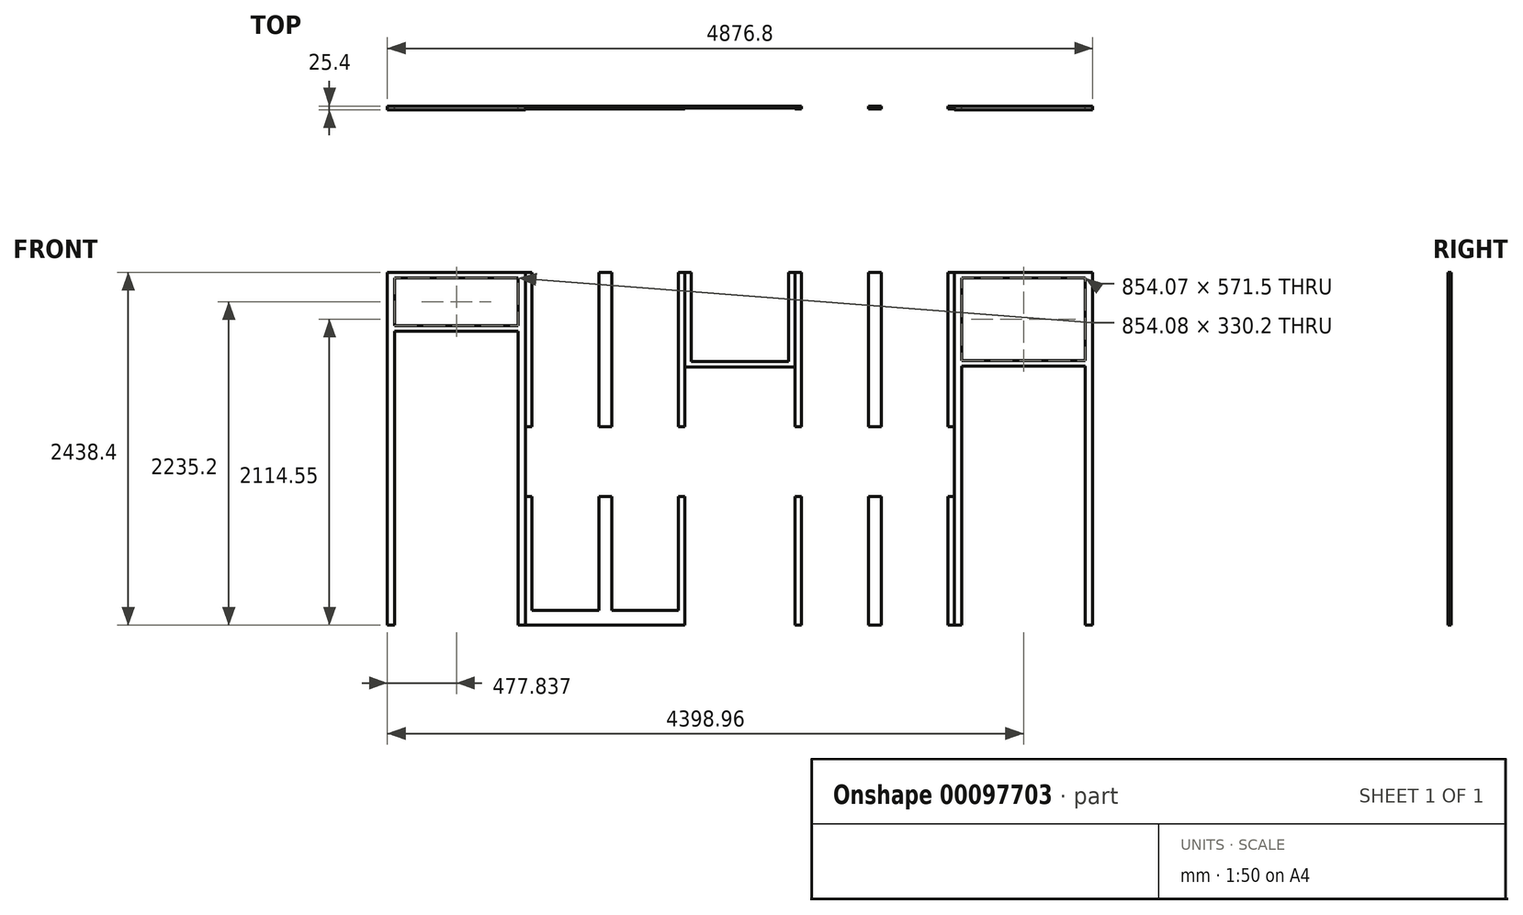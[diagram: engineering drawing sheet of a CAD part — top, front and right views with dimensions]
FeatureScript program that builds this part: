
annotation { "Feature Type Name" : "Feature", "Feature Type Description" : "" }
export const myFeature = defineFeature(function(context is Context, id is Id, definition is map)
    precondition{}
    {
        {
            var Q0;
            Q0=qCreatedBy(makeId("Front.planeOp"),FACE);
            var sketch = newSketch(context, id + "F0", { "sketchPlane" : qUnion([Q0])});
            skLineSegment(sketch, "E0.bottom", {"start": v(0, 0) * mm, "end": v(4876.8, 0) * mm});
            skLineSegment(sketch, "E0.top", {"start": v(0, 2438.4) * mm, "end": v(4876.8, 2438.4) * mm});
            skLineSegment(sketch, "E0.left", {"start": v(0, 0) * mm, "end": v(0, 2438.4) * mm});
            skLineSegment(sketch, "E0.right", {"start": v(4876.8, 0) * mm, "end": v(4876.8, 2438.4) * mm});
            skLineSegment(sketch, "E1", {"start": v(3971.92, 2438.4) * mm, "end": v(3971.92, 0) * mm});
            skLineSegment(sketch, "E2.0", {"start": v(3921.12, 2438.4) * mm, "end": v(3921.12, 0) * mm});
            skLineSegment(sketch, "E3.0", {"start": v(4826, 0) * mm, "end": v(4826, 2438.4) * mm});
            skLineSegment(sketch, "E4", {"start": v(3971.92, 1790.7) * mm, "end": v(4826, 1790.7) * mm});
            skLineSegment(sketch, "E5.0", {"start": v(3971.92, 1828.8) * mm, "end": v(4826, 1828.8) * mm});
            skLineSegment(sketch, "E6", {"start": v(3971.93, 2400.3) * mm, "end": v(4826, 2400.3) * mm});
            skLineSegment(sketch, "E7", {"start": v(3876.67, 0) * mm, "end": v(3876.67, 889) * mm});
            skLineSegment(sketch, "E8", {"start": v(3876.67, 889) * mm, "end": v(3921.13, 889) * mm});
            skLineSegment(sketch, "E9", {"start": v(2438.4, 0) * mm, "end": v(2438.4, 2578.54) * mm, "construction": true});
            skLineSegment(sketch, "E10", {"start": v(2057.4, 0) * mm, "end": v(2057.4, 914.4) * mm});
            skLineSegment(sketch, "E11", {"start": v(2057.4, 914.4) * mm, "end": v(2819.4, 914.4) * mm});
            skLineSegment(sketch, "E12", {"start": v(2819.4, 914.4) * mm, "end": v(2819.4, 0) * mm});
            skLineSegment(sketch, "E13", {"start": v(2819.4, 889) * mm, "end": v(2863.85, 889) * mm});
            skLineSegment(sketch, "E14", {"start": v(2863.85, 889) * mm, "end": v(2863.85, 0) * mm});
            skLineSegment(sketch, "E15", {"start": v(3414.71, 0) * mm, "end": v(3414.71, 889) * mm});
            skLineSegment(sketch, "E16", {"start": v(3325.81, 889) * mm, "end": v(3414.71, 889) * mm});
            skLineSegment(sketch, "E17", {"start": v(3325.81, 889) * mm, "end": v(3325.81, 0) * mm});
            skLineSegment(sketch, "E18", {"start": v(50.8, 0) * mm, "end": v(50.8, 2438.4) * mm});
            skLineSegment(sketch, "E19", {"start": v(50.8, 2032) * mm, "end": v(904.87, 2032) * mm});
            skLineSegment(sketch, "E20", {"start": v(904.87, 2438.4) * mm, "end": v(904.87, 0) * mm});
            skLineSegment(sketch, "E21.0", {"start": v(50.8, 2070.1) * mm, "end": v(904.87, 2070.1) * mm});
            skLineSegment(sketch, "E22.0", {"start": v(955.67, 2438.4) * mm, "end": v(955.67, 0) * mm});
            skLineSegment(sketch, "E23", {"start": v(1000.12, 101.6) * mm, "end": v(1000.12, 889) * mm});
            skLineSegment(sketch, "E24", {"start": v(1000.12, 889) * mm, "end": v(955.68, 889) * mm});
            skLineSegment(sketch, "E25", {"start": v(2012.95, 0) * mm, "end": v(2012.95, 889) * mm});
            skLineSegment(sketch, "E26", {"start": v(2012.95, 889) * mm, "end": v(2057.4, 889) * mm});
            skLineSegment(sketch, "E27", {"start": v(1550.99, 101.6) * mm, "end": v(1550.99, 889) * mm});
            skLineSegment(sketch, "E28", {"start": v(1462.09, 889) * mm, "end": v(1550.99, 889) * mm});
            skLineSegment(sketch, "E29", {"start": v(1462.09, 889) * mm, "end": v(1462.09, 101.6) * mm});
            skLineSegment(sketch, "E30", {"start": v(1000.12, 889) * mm, "end": v(1550.99, 889) * mm, "construction": true});
            skLineSegment(sketch, "E31", {"start": v(1462.09, 889) * mm, "end": v(2012.95, 889) * mm, "construction": true});
            skLineSegment(sketch, "E32", {"start": v(2863.85, 889) * mm, "end": v(3325.81, 889) * mm, "construction": true});
            skLineSegment(sketch, "E33", {"start": v(3414.71, 889) * mm, "end": v(3876.67, 889) * mm, "construction": true});
            skLineSegment(sketch, "E34", {"start": v(1000.12, 101.6) * mm, "end": v(2012.95, 101.6) * mm});
            skLineSegment(sketch, "E35", {"start": v(50.8, 2400.3) * mm, "end": v(904.87, 2400.3) * mm});
            skPoint(sketch, "E36.orphan", {"position": v(1462.09, 0) * mm});
            skLineSegment(sketch, "E37", {"start": v(1000.12, 2438.4) * mm, "end": v(1000.12, 1371.6) * mm});
            skLineSegment(sketch, "E38", {"start": v(1000.12, 1371.6) * mm, "end": v(955.67, 1371.6) * mm});
            skLineSegment(sketch, "E39", {"start": v(1462.09, 1371.6) * mm, "end": v(1462.09, 2438.4) * mm});
            skLineSegment(sketch, "E40", {"start": v(1462.09, 1371.6) * mm, "end": v(1550.99, 1371.6) * mm});
            skLineSegment(sketch, "E41", {"start": v(1550.99, 1371.6) * mm, "end": v(1550.99, 2438.4) * mm});
            skLineSegment(sketch, "E42", {"start": v(2012.95, 1371.6) * mm, "end": v(2012.95, 2438.4) * mm});
            skLineSegment(sketch, "E43", {"start": v(2012.95, 1371.6) * mm, "end": v(2057.4, 1371.6) * mm});
            skLineSegment(sketch, "E44", {"start": v(2057.4, 1371.6) * mm, "end": v(2057.4, 2438.4) * mm});
            skLineSegment(sketch, "E45", {"start": v(2057.4, 1784.35) * mm, "end": v(2819.4, 1784.35) * mm});
            skLineSegment(sketch, "E46.0", {"start": v(2057.4, 1822.45) * mm, "end": v(2819.4, 1822.45) * mm});
            skLineSegment(sketch, "E47", {"start": v(2819.4, 1371.6) * mm, "end": v(2819.4, 2438.4) * mm});
            skLineSegment(sketch, "E48", {"start": v(2819.4, 1371.6) * mm, "end": v(2863.85, 1371.6) * mm});
            skLineSegment(sketch, "E49", {"start": v(2863.85, 1371.6) * mm, "end": v(2863.85, 2438.4) * mm});
            skLineSegment(sketch, "E50", {"start": v(2774.95, 1822.45) * mm, "end": v(2774.95, 2438.4) * mm});
            skLineSegment(sketch, "E51", {"start": v(2101.85, 1822.45) * mm, "end": v(2101.85, 2438.4) * mm});
            skLineSegment(sketch, "E52", {"start": v(3325.81, 1371.6) * mm, "end": v(3325.81, 2438.4) * mm});
            skLineSegment(sketch, "E53", {"start": v(3325.81, 1371.6) * mm, "end": v(3414.71, 1371.6) * mm});
            skLineSegment(sketch, "E54", {"start": v(3414.71, 1371.6) * mm, "end": v(3414.71, 2438.4) * mm});
            skLineSegment(sketch, "E55", {"start": v(3876.67, 1371.6) * mm, "end": v(3876.67, 2438.4) * mm});
            skLineSegment(sketch, "E56", {"start": v(3876.67, 1371.6) * mm, "end": v(3921.12, 1371.6) * mm});
            skSolve(sketch);
        }
        {
            var Q0;
            {var subQ4=sQuery(id+"F0.wireOp",EDGE,"E0.left");Q0=makeQuery(id+"F0.imprint","IMPRINT",FACE,{"disambiguationData":[TD([[makeQuery(id+"F0.imprint","IMPRINT",EDGE,{"derivedFrom":subQ4}),-1.0]])]});}
            var Q1;
            {var subQ0=sQuery(id+"F0.wireOp",EDGE,"E19");Q1=makeQuery(id+"F0.imprint","IMPRINT",FACE,{"disambiguationData":[TD([[makeQuery(id+"F0.imprint","IMPRINT",EDGE,{"derivedFrom":subQ0}),1.0]])]});}
            var Q2;
            {var subQ5=sQuery(id+"F0.wireOp",EDGE,"E35");Q2=makeQuery(id+"F0.imprint","IMPRINT",FACE,{"disambiguationData":[TD([[makeQuery(id+"F0.imprint","IMPRINT",EDGE,{"derivedFrom":subQ5}),1.0]])]});}
            var Q3;
            {var subQ0=sQuery(id+"F0.wireOp",EDGE,"E20");var subQ8=sQuery(id+"F0.wireOp",EDGE,"E0.bottom");var subQ11=makeQuery(id+"F0.imprint","INTERSECT",VERTEX,{"derivedFrom":[subQ8,subQ0]});Q3=makeQuery(id+"F0.imprint","IMPRINT",FACE,{"disambiguationData":[TD([[makeQuery(id+"F0.imprint","IMPRINT",EDGE,{"disambiguationData":[TD([[subQ11,-1.0]])],"derivedFrom":subQ8}),1.0]])]});}
            var Q4;
            {var subQ0=sQuery(id+"F0.wireOp",EDGE,"E1");var subQ7=sQuery(id+"F0.wireOp",EDGE,"E0.bottom");var subQ10=makeQuery(id+"F0.imprint","INTERSECT",VERTEX,{"derivedFrom":[subQ7,subQ0]});Q4=makeQuery(id+"F0.imprint","IMPRINT",FACE,{"disambiguationData":[TD([[makeQuery(id+"F0.imprint","IMPRINT",EDGE,{"disambiguationData":[TD([[subQ10,1.0]])],"derivedFrom":subQ7}),1.0]])]});}
            var Q5;
            {var subQ0=sQuery(id+"F0.wireOp",EDGE,"E4");Q5=makeQuery(id+"F0.imprint","IMPRINT",FACE,{"disambiguationData":[TD([[makeQuery(id+"F0.imprint","IMPRINT",EDGE,{"derivedFrom":subQ0}),1.0]])]});}
            var Q6;
            {var subQ5=sQuery(id+"F0.wireOp",EDGE,"E6");Q6=makeQuery(id+"F0.imprint","IMPRINT",FACE,{"disambiguationData":[TD([[makeQuery(id+"F0.imprint","IMPRINT",EDGE,{"derivedFrom":subQ5}),1.0]])]});}
            var Q7;
            {var subQ0=sQuery(id+"F0.wireOp",EDGE,"E0.right");Q7=makeQuery(id+"F0.imprint","IMPRINT",FACE,{"disambiguationData":[TD([[makeQuery(id+"F0.imprint","IMPRINT",EDGE,{"derivedFrom":subQ0}),1.0]])]});}
            extrude(context, id + "F1", {"entities" : qUnion([Q0, Q1, Q2, Q3, Q4, Q5, Q6, Q7]), "depth" : 25.4 * mm});
        }
        {
            var Q0;
            {var subQ3=sQuery(id+"F0.wireOp",EDGE,"E37");Q0=makeQuery(id+"F0.imprint","IMPRINT",FACE,{"disambiguationData":[TD([[makeQuery(id+"F0.imprint","IMPRINT",EDGE,{"derivedFrom":subQ3}),-1.0]])]});}
            var Q1;
            {var subQ0=sQuery(id+"F0.wireOp",EDGE,"E39");Q1=makeQuery(id+"F0.imprint","IMPRINT",FACE,{"disambiguationData":[TD([[makeQuery(id+"F0.imprint","IMPRINT",EDGE,{"derivedFrom":subQ0}),-1.0]])]});}
            var Q2;
            {var subQ3=sQuery(id+"F0.wireOp",EDGE,"E42");Q2=makeQuery(id+"F0.imprint","IMPRINT",FACE,{"disambiguationData":[TD([[makeQuery(id+"F0.imprint","IMPRINT",EDGE,{"derivedFrom":subQ3}),-1.0]])]});}
            var Q3;
            {var subQ6=sQuery(id+"F0.wireOp",EDGE,"E48");Q3=makeQuery(id+"F0.imprint","IMPRINT",FACE,{"disambiguationData":[TD([[makeQuery(id+"F0.imprint","IMPRINT",EDGE,{"derivedFrom":subQ6}),1.0]])]});}
            var Q4;
            {var subQ0=sQuery(id+"F0.wireOp",EDGE,"E52");Q4=makeQuery(id+"F0.imprint","IMPRINT",FACE,{"disambiguationData":[TD([[makeQuery(id+"F0.imprint","IMPRINT",EDGE,{"derivedFrom":subQ0}),-1.0]])]});}
            var Q5;
            {var subQ3=sQuery(id+"F0.wireOp",EDGE,"E55");Q5=makeQuery(id+"F0.imprint","IMPRINT",FACE,{"disambiguationData":[TD([[makeQuery(id+"F0.imprint","IMPRINT",EDGE,{"derivedFrom":subQ3}),-1.0]])]});}
            var Q6;
            {var subQ1=sQuery(id+"F0.wireOp",EDGE,"E23");Q6=makeQuery(id+"F0.imprint","IMPRINT",FACE,{"disambiguationData":[TD([[makeQuery(id+"F0.imprint","IMPRINT",EDGE,{"derivedFrom":subQ1}),1.0]])]});}
            var Q7;
            {var subQ0=sQuery(id+"F0.wireOp",EDGE,"E27");Q7=makeQuery(id+"F0.imprint","IMPRINT",FACE,{"disambiguationData":[TD([[makeQuery(id+"F0.imprint","IMPRINT",EDGE,{"derivedFrom":subQ0}),1.0]])]});}
            var Q8;
            {var subQ0=sQuery(id+"F0.wireOp",EDGE,"E26");Q8=makeQuery(id+"F0.imprint","IMPRINT",FACE,{"disambiguationData":[TD([[makeQuery(id+"F0.imprint","IMPRINT",EDGE,{"derivedFrom":subQ0}),-1.0]])]});}
            var Q9;
            {var subQ4=sQuery(id+"F0.wireOp",EDGE,"E13");Q9=makeQuery(id+"F0.imprint","IMPRINT",FACE,{"disambiguationData":[TD([[makeQuery(id+"F0.imprint","IMPRINT",EDGE,{"derivedFrom":subQ4}),-1.0]])]});}
            var Q10;
            {var subQ0=sQuery(id+"F0.wireOp",EDGE,"E15");Q10=makeQuery(id+"F0.imprint","IMPRINT",FACE,{"disambiguationData":[TD([[makeQuery(id+"F0.imprint","IMPRINT",EDGE,{"derivedFrom":subQ0}),1.0]])]});}
            var Q11;
            {var subQ3=sQuery(id+"F0.wireOp",EDGE,"E7");Q11=makeQuery(id+"F0.imprint","IMPRINT",FACE,{"disambiguationData":[TD([[makeQuery(id+"F0.imprint","IMPRINT",EDGE,{"derivedFrom":subQ3}),-1.0]])]});}
            extrude(context, id + "F2", {"entities" : qUnion([Q0, Q1, Q2, Q3, Q4, Q5, Q6, Q7, Q8, Q9, Q10, Q11]), "depth" : 19.05 * mm});
        }
        {
            var Q0;
            {var subQ3=sQuery(id+"F0.wireOp",EDGE,"E51");Q0=makeQuery(id+"F0.imprint","IMPRINT",FACE,{"disambiguationData":[TD([[makeQuery(id+"F0.imprint","IMPRINT",EDGE,{"derivedFrom":subQ3}),1.0]])]});}
            var Q1;
            {var subQ5=sQuery(id+"F0.wireOp",EDGE,"E45");Q1=makeQuery(id+"F0.imprint","IMPRINT",FACE,{"disambiguationData":[TD([[makeQuery(id+"F0.imprint","IMPRINT",EDGE,{"derivedFrom":subQ5}),1.0]])]});}
            var Q2;
            {var subQ3=sQuery(id+"F0.wireOp",EDGE,"E50");Q2=makeQuery(id+"F0.imprint","IMPRINT",FACE,{"disambiguationData":[TD([[makeQuery(id+"F0.imprint","IMPRINT",EDGE,{"derivedFrom":subQ3}),-1.0]])]});}
            extrude(context, id + "F3", {"entities" : qUnion([Q0, Q1, Q2]), "depth" : 12.7 * mm});
        }
    });
